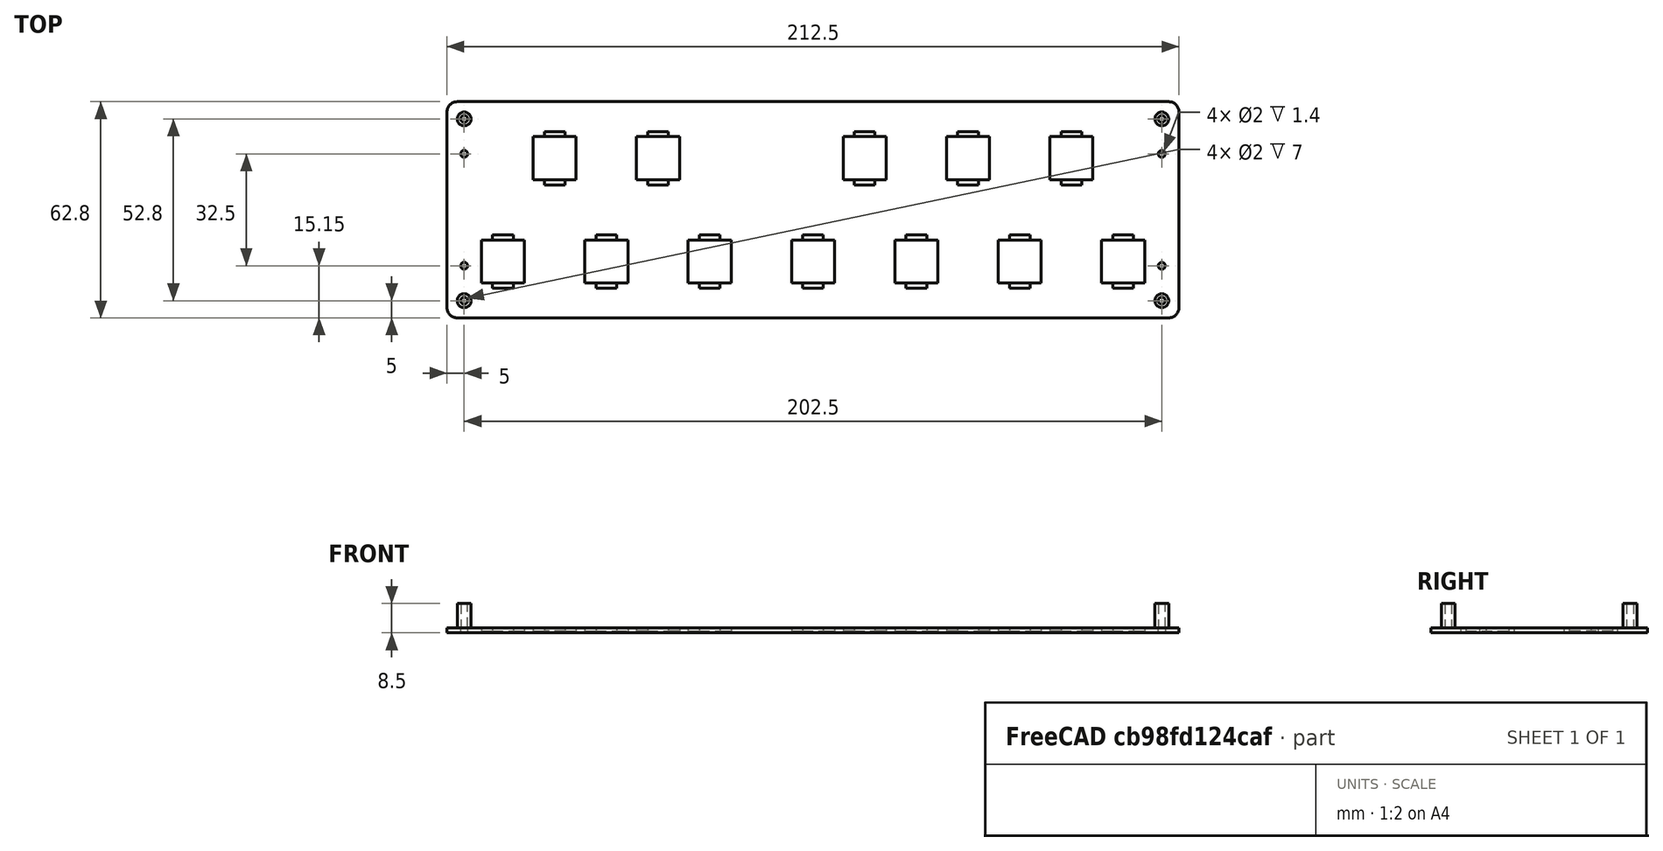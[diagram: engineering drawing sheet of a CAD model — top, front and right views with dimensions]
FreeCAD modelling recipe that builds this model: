
FCSTD DOCUMENT  (FreeCAD 0.20R28671 (Git))
Label: soporte botones
License: All rights reserved
LicenseURL: http://en.wikipedia.org/wiki/All_rights_reserved
objects: TechDraw::DrawViewDimension×21, Sketcher::SketchObject×5, PartDesign::Pocket×3, PartDesign::Pad×2, TechDraw::DrawProjGroupItem×2, PartDesign::Fillet×1, PartDesign::Body×1, TechDraw::DrawSVGTemplate×1, TechDraw::DrawProjGroup×1, TechDraw::DrawPage×1
note: 18 computed .brp shape members not serialized (recipe doc carries the construction recipe); baked Part::Feature solids carry a one-line shape summary decoded from their .brp

FEATURE [Sketcher::SketchObject] Sketch
  FullyConstrained = true
  MapMode = 5
  Support = -> [XY_Plane]
  sketch-geometry (75):
    g0: LineSegment StartX=0 StartY=0 StartZ=0 EndX=30 EndY=0 EndZ=0
    g1: LineSegment StartX=30 StartY=0 StartZ=0 EndX=30 EndY=30 EndZ=0
    g2: LineSegment StartX=0 StartY=30 StartZ=0 EndX=0 EndY=0 EndZ=0
    g3: LineSegment StartX=0 StartY=30 StartZ=0 EndX=15 EndY=30 EndZ=0
    g4: LineSegment StartX=15 StartY=30 StartZ=0 EndX=30 EndY=30 EndZ=0
    g5: LineSegment StartX=6.25 StartY=-6.25 StartZ=0 EndX=6.25 EndY=6.25 EndZ=0
    g6: LineSegment StartX=6.25 StartY=6.25 StartZ=0 EndX=-6.25 EndY=6.25 EndZ=0
    g7: LineSegment StartX=-6.25 StartY=6.25 StartZ=0 EndX=-6.25 EndY=-6.25 EndZ=0
    g8: LineSegment StartX=-6.25 StartY=-6.25 StartZ=0 EndX=6.25 EndY=-6.25 EndZ=0
    g9: Circle CenterX=0 CenterY=0 CenterZ=0 NormalX=0 NormalY=0 NormalZ=1 AngleXU=0 Radius=8.83883
    g10: LineSegment StartX=23.75 StartY=-6.25 StartZ=0 EndX=36.25 EndY=-6.25 EndZ=0
    g11: LineSegment StartX=23.75 StartY=6.25 StartZ=0 EndX=23.75 EndY=-6.25 EndZ=0
    g12: LineSegment StartX=36.25 StartY=6.25 StartZ=0 EndX=23.75 EndY=6.25 EndZ=0
    g13: LineSegment StartX=36.25 StartY=-6.25 StartZ=0 EndX=36.25 EndY=6.25 EndZ=0
    g14: LineSegment StartX=-6.25 StartY=-6.25 StartZ=0 EndX=23.75 EndY=-6.25 EndZ=0
    g15: LineSegment StartX=53.75 StartY=-6.25 StartZ=0 EndX=66.25 EndY=-6.25 EndZ=0
    g16: LineSegment StartX=53.75 StartY=6.25 StartZ=0 EndX=53.75 EndY=-6.25 EndZ=0
    g17: LineSegment StartX=66.25 StartY=6.25 StartZ=0 EndX=53.75 EndY=6.25 EndZ=0
    g18: LineSegment StartX=66.25 StartY=-6.25 StartZ=0 EndX=66.25 EndY=6.25 EndZ=0
    g19: LineSegment StartX=23.75 StartY=-6.25 StartZ=0 EndX=53.75 EndY=-6.25 EndZ=0
    g20: LineSegment StartX=83.75 StartY=-6.25 StartZ=0 EndX=96.25 EndY=-6.25 EndZ=0
    g21: LineSegment StartX=83.75 StartY=6.25 StartZ=0 EndX=83.75 EndY=-6.25 EndZ=0
    g22: LineSegment StartX=96.25 StartY=6.25 StartZ=0 EndX=83.75 EndY=6.25 EndZ=0
    g23: LineSegment StartX=96.25 StartY=-6.25 StartZ=0 EndX=96.25 EndY=6.25 EndZ=0
    g24: LineSegment StartX=53.75 StartY=-6.25 StartZ=0 EndX=83.75 EndY=-6.25 EndZ=0
    g25: LineSegment StartX=113.75 StartY=-6.25 StartZ=0 EndX=126.25 EndY=-6.25 EndZ=0
    g26: LineSegment StartX=113.75 StartY=6.25 StartZ=0 EndX=113.75 EndY=-6.25 EndZ=0
    g27: LineSegment StartX=126.25 StartY=6.25 StartZ=0 EndX=113.75 EndY=6.25 EndZ=0
    g28: LineSegment StartX=126.25 StartY=-6.25 StartZ=0 EndX=126.25 EndY=6.25 EndZ=0
    g29: LineSegment StartX=83.75 StartY=-6.25 StartZ=0 EndX=113.75 EndY=-6.25 EndZ=0
    g30: LineSegment StartX=143.75 StartY=-6.25 StartZ=0 EndX=156.25 EndY=-6.25 EndZ=0
    g31: LineSegment StartX=143.75 StartY=6.25 StartZ=0 EndX=143.75 EndY=-6.25 EndZ=0
    g32: LineSegment StartX=156.25 StartY=6.25 StartZ=0 EndX=143.75 EndY=6.25 EndZ=0
    g33: LineSegment StartX=156.25 StartY=-6.25 StartZ=0 EndX=156.25 EndY=6.25 EndZ=0
    g34: LineSegment StartX=113.75 StartY=-6.25 StartZ=0 EndX=143.75 EndY=-6.25 EndZ=0
    g35: LineSegment StartX=173.75 StartY=-6.25 StartZ=0 EndX=186.25 EndY=-6.25 EndZ=0
    g36: LineSegment StartX=173.75 StartY=6.25 StartZ=0 EndX=173.75 EndY=-6.25 EndZ=0
    g37: LineSegment StartX=186.25 StartY=6.25 StartZ=0 EndX=173.75 EndY=6.25 EndZ=0
    g38: LineSegment StartX=186.25 StartY=-6.25 StartZ=0 EndX=186.25 EndY=6.25 EndZ=0
    g39: LineSegment StartX=143.75 StartY=-6.25 StartZ=0 EndX=173.75 EndY=-6.25 EndZ=0
    g40: LineSegment StartX=8.75 StartY=23.75 StartZ=0 EndX=8.75 EndY=36.25 EndZ=0
    g41: LineSegment StartX=8.75 StartY=36.25 StartZ=0 EndX=21.25 EndY=36.25 EndZ=0
    g42: LineSegment StartX=21.25 StartY=36.25 StartZ=0 EndX=21.25 EndY=23.75 EndZ=0
    g43: LineSegment StartX=21.25 StartY=23.75 StartZ=0 EndX=8.75 EndY=23.75 EndZ=0
    g44: GeomPoint X=15 Y=30 Z=0
    g45: LineSegment StartX=30 StartY=30 StartZ=0 EndX=45 EndY=30 EndZ=0
    g46: LineSegment StartX=45 StartY=30 StartZ=0 EndX=60 EndY=30 EndZ=0
    g47: LineSegment StartX=38.75 StartY=36.25 StartZ=0 EndX=38.75 EndY=23.75 EndZ=0
    g48: LineSegment StartX=38.75 StartY=23.75 StartZ=0 EndX=51.25 EndY=23.75 EndZ=0
    g49: LineSegment StartX=51.25 StartY=23.75 StartZ=0 EndX=51.25 EndY=36.25 EndZ=0
    g50: LineSegment StartX=51.25 StartY=36.25 StartZ=0 EndX=38.75 EndY=36.25 EndZ=0
    g51: GeomPoint X=45 Y=30 Z=0
    g52: LineSegment StartX=90 StartY=30 StartZ=0 EndX=105 EndY=30 EndZ=0
    g53: LineSegment StartX=105 StartY=30 StartZ=0 EndX=120 EndY=30 EndZ=0
    g54: LineSegment StartX=120 StartY=30 StartZ=0 EndX=135 EndY=30 EndZ=0
    g55: LineSegment StartX=135 StartY=30 StartZ=0 EndX=150 EndY=30 EndZ=0
    g56: LineSegment StartX=150 StartY=30 StartZ=0 EndX=165 EndY=30 EndZ=0
    g57: LineSegment StartX=165 StartY=30 StartZ=0 EndX=180 EndY=30 EndZ=0
    g58: LineSegment StartX=90 StartY=30 StartZ=0 EndX=75 EndY=30 EndZ=0
    g59: LineSegment StartX=75 StartY=30 StartZ=0 EndX=60 EndY=30 EndZ=0
    g60: LineSegment StartX=98.75 StartY=36.25 StartZ=0 EndX=98.75 EndY=23.75 EndZ=0
    g61: LineSegment StartX=98.75 StartY=23.75 StartZ=0 EndX=111.25 EndY=23.75 EndZ=0
    g62: LineSegment StartX=111.25 StartY=23.75 StartZ=0 EndX=111.25 EndY=36.25 EndZ=0
    g63: LineSegment StartX=111.25 StartY=36.25 StartZ=0 EndX=98.75 EndY=36.25 EndZ=0
    g64: GeomPoint X=105 Y=30 Z=0
    g65: LineSegment StartX=128.75 StartY=36.25 StartZ=0 EndX=128.75 EndY=23.75 EndZ=0
    g66: LineSegment StartX=128.75 StartY=23.75 StartZ=0 EndX=141.25 EndY=23.75 EndZ=0
    g67: LineSegment StartX=141.25 StartY=23.75 StartZ=0 EndX=141.25 EndY=36.25 EndZ=0
    g68: LineSegment StartX=141.25 StartY=36.25 StartZ=0 EndX=128.75 EndY=36.25 EndZ=0
    g69: GeomPoint X=135 Y=30 Z=0
    g70: LineSegment StartX=158.75 StartY=36.25 StartZ=0 EndX=158.75 EndY=23.75 EndZ=0
    g71: LineSegment StartX=158.75 StartY=23.75 StartZ=0 EndX=171.25 EndY=23.75 EndZ=0
    g72: LineSegment StartX=171.25 StartY=23.75 StartZ=0 EndX=171.25 EndY=36.25 EndZ=0
    g73: LineSegment StartX=171.25 StartY=36.25 StartZ=0 EndX=158.75 EndY=36.25 EndZ=0
    g74: GeomPoint X=165 Y=30 Z=0
  constraints (202):
    c: Coincident(g0,g1)
    c: Coincident(g2,g0)
    c: Horizontal(g0)
    c: Vertical(g1)
    c: Vertical(g2)
    c: Coincident(g0,g-1)
    c: Coincident(g3,g2)
    c: Horizontal(g3)
    c: Coincident(g4,g3)
    c: Coincident(g4,g1)
    c: Horizontal(g4)
    c: Equal(g4,g3)
    c: Coincident(g5,g6)
    c: Coincident(g6,g7)
    c: Coincident(g7,g8)
    c: Coincident(g8,g5)
    c: Equal(g5,g6)
    c: Equal(g5,g7)
    c: Equal(g5,g8)
    c: PointOnObject(g5,g9)
    c: PointOnObject(g6,g9)
    c: PointOnObject(g7,g9)
    c: PointOnObject(g8,g9)
    c: Coincident(g9,g-1)
    c: Horizontal(g6)
    c: DistanceY(g7,g7) = 12.5
    c: Coincident(g13,g12)
    c: Coincident(g12,g11)
    c: Coincident(g11,g10)
    c: Coincident(g10,g13)
    c: Equal(g13,g12)
    c: Equal(g13,g11)
    c: Equal(g13,g10)
    c: Horizontal(g12)
    c: Coincident(g8,g14)
    c: Coincident(g10,g14)
    c: Distance(g14) = 30
    c: Coincident(g18,g17)
    c: Coincident(g17,g16)
    c: Coincident(g16,g15)
    c: Coincident(g15,g18)
    c: Equal(g18,g17)
    c: Equal(g18,g16)
    c: Equal(g18,g15)
    c: Horizontal(g17)
    c: Coincident(g10,g19)
    c: Coincident(g15,g19)
    c: Equal(g14,g19)
    c: Parallel(g19,g14)
    c: Coincident(g23,g22)
    c: Coincident(g22,g21)
    c: Coincident(g21,g20)
    c: Coincident(g20,g23)
    c: Equal(g23,g22)
    c: Equal(g23,g21)
    c: Equal(g23,g20)
    c: Horizontal(g22)
    c: Coincident(g15,g24)
    c: Coincident(g20,g24)
    c: Equal(g14,g24)
    c: Parallel(g24,g14)
    c: Coincident(g28,g27)
    c: Coincident(g27,g26)
    c: Coincident(g26,g25)
    c: Coincident(g25,g28)
    c: Equal(g28,g27)
    c: Equal(g28,g26)
    c: Equal(g28,g25)
    c: Horizontal(g27)
    c: Coincident(g20,g29)
    c: Coincident(g25,g29)
    c: Equal(g14,g29)
    c: Parallel(g29,g14)
    c: Coincident(g33,g32)
    c: Coincident(g32,g31)
    c: Coincident(g31,g30)
    c: Coincident(g30,g33)
    c: Equal(g33,g32)
    c: Equal(g33,g31)
    c: Equal(g33,g30)
    c: Horizontal(g32)
    c: Coincident(g25,g34)
    c: Coincident(g30,g34)
    c: Equal(g14,g34)
    c: Parallel(g34,g14)
    c: Coincident(g38,g37)
    c: Coincident(g37,g36)
    c: Coincident(g36,g35)
    c: Coincident(g35,g38)
    c: Equal(g38,g37)
    c: Equal(g38,g36)
    c: Equal(g38,g35)
    c: Horizontal(g37)
    c: Coincident(g30,g39)
    c: Coincident(g35,g39)
    c: Equal(g14,g39)
    c: Parallel(g39,g14)
    c: Horizontal(g19)
    c: Vertical(g11)
    c: Vertical(g16)
    c: Vertical(g21)
    c: Vertical(g26)
    c: Vertical(g31)
    c: Vertical(g36)
    c: Equal(g5,g11)
    c: Equal(g11,g16)
    c: Equal(g16,g21)
    c: Equal(g21,g26)
    c: Equal(g26,g31)
    c: Equal(g31,g36)
    c: Equal(g14,g1)
    c: Equal(g0,g2)
    c: Coincident(g40,g41)
    c: Coincident(g41,g42)
    c: Coincident(g42,g43)
    c: Coincident(g43,g40)
    c: Horizontal(g41)
    c: Horizontal(g43)
    c: Vertical(g40)
    c: Vertical(g42)
    c: Symmetric(g41,g40,g44)
    c: Coincident(g44,g3)
    c: Equal(g43,g12)
    c: Equal(g41,g42)
    c: Horizontal(g45)
    c: Coincident(g46,g45)
    c: Equal(g46,g45)
    c: Equal(g45,g3)
    c: Coincident(g45,g1)
    c: Horizontal(g46)
    c: Coincident(g47,g48)
    c: Coincident(g48,g49)
    c: Coincident(g49,g50)
    c: Coincident(g50,g47)
    c: Horizontal(g48)
    c: Horizontal(g50)
    c: Vertical(g47)
    c: Vertical(g49)
    c: Symmetric(g48,g47,g51)
    c: Coincident(g51,g45)
    c: Equal(g42,g50)
    c: Equal(g47,g50)
    c: Horizontal(g52)
    c: Coincident(g52,g53)
    c: Horizontal(g53)
    c: Coincident(g53,g54)
    c: Horizontal(g54)
    c: Coincident(g54,g55)
    c: Horizontal(g55)
    c: Coincident(g55,g56)
    c: Horizontal(g56)
    c: Coincident(g56,g57)
    c: Horizontal(g57)
    c: Equal(g46,g52)
    c: Equal(g52,g53)
    c: Equal(g53,g54)
    c: Equal(g54,g55)
    c: Equal(g55,g56)
    c: Equal(g56,g57)
    c: Horizontal(g52,g46)
    c: Coincident(g52,g58)
    c: Horizontal(g58)
    c: Coincident(g58,g59)
    c: Coincident(g59,g46)
    c: Equal(g59,g58)
    c: Equal(g58,g52)
    c: Coincident(g60,g61)
    c: Coincident(g61,g62)
    c: Coincident(g62,g63)
    c: Coincident(g63,g60)
    c: Horizontal(g61)
    c: Horizontal(g63)
    c: Vertical(g60)
    c: Vertical(g62)
    c: Symmetric(g61,g60,g64)
    c: Coincident(g65,g66)
    c: Coincident(g66,g67)
    c: Coincident(g67,g68)
    c: Coincident(g68,g65)
    c: Horizontal(g66)
    c: Horizontal(g68)
    c: Vertical(g65)
    c: Vertical(g67)
    c: Symmetric(g66,g65,g69)
    c: Coincident(g69,g54)
    c: Coincident(g70,g71)
    c: Coincident(g71,g72)
    c: Coincident(g72,g73)
    c: Coincident(g73,g70)
    c: Horizontal(g71)
    c: Horizontal(g73)
    c: Vertical(g70)
    c: Vertical(g72)
    c: Symmetric(g71,g70,g74)
    c: Coincident(g74,g56)
    c: Equal(g63,g62)
    c: Equal(g62,g68)
    c: Equal(g68,g65)
    c: Equal(g65,g73)
    c: Equal(g73,g70)
    c: Equal(g70,g13)
    c: Coincident(g64,g52)
FEATURE [Sketcher::SketchObject] Sketch001
  ExternalGeometry = -> [Sketch]
  FullyConstrained = true
  MapMode = 5
  Support = -> [XY_Plane]
  sketch-geometry (8):
    g0: LineSegment StartX=-16.25 StartY=46.4 StartZ=0 EndX=196.25 EndY=46.4 EndZ=0
    g1: LineSegment StartX=196.25 StartY=46.4 StartZ=0 EndX=196.25 EndY=-16.4 EndZ=0
    g2: LineSegment StartX=196.25 StartY=-16.4 StartZ=0 EndX=-16.25 EndY=-16.4 EndZ=0
    g3: LineSegment StartX=-16.25 StartY=-16.4 StartZ=0 EndX=-16.25 EndY=46.4 EndZ=0
    g4: LineSegment StartX=-6.25 StartY=-6.25 StartZ=0 EndX=-6.25 EndY=-16.4 EndZ=0
    g5: LineSegment StartX=-6.25 StartY=-6.25 StartZ=0 EndX=-16.25 EndY=-6.25 EndZ=0
    g6: LineSegment StartX=186.25 StartY=-6.25 StartZ=0 EndX=196.25 EndY=-6.25 EndZ=0
    g7: LineSegment StartX=171.25 StartY=36.25 StartZ=0 EndX=171.25 EndY=46.4 EndZ=0
  constraints (24):
    c: Coincident(g0,g1)
    c: Coincident(g1,g2)
    c: Coincident(g2,g3)
    c: Coincident(g3,g0)
    c: Horizontal(g0)
    c: Horizontal(g2)
    c: Vertical(g1)
    c: Vertical(g3)
    c: Coincident(g4,g-3)
    c: PointOnObject(g4,g2)
    c: Vertical(g4)
    c: Coincident(g5,g4)
    c: PointOnObject(g5,g3)
    c: Horizontal(g5)
    c: Coincident(g6,g-4)
    c: PointOnObject(g6,g1)
    c: Coincident(g7,g-6)
    c: PointOnObject(g7,g0)
    c: Vertical(g7)
    c: Horizontal(g6)
    c: DistanceY(g4,g4) = 10.15
    c: DistanceX(g5,g4) = 10
    c: Equal(g6,g5)
    c: Equal(g4,g7)
FEATURE [PartDesign::Pad] Pad
  Direction = (0,0,1)
  Length = 1.5
  Length2 = 100
  Profile = -> Sketch001
  ReferenceAxis = -> Sketch001 [N_Axis]
  Reversed = true
  Type = 0
FEATURE [PartDesign::Pocket] Pocket
  BaseFeature = -> Pad
  Direction = (0,0,-1)
  Length = 1
  Length2 = 100
  Profile = -> Sketch
  Type = 0
FEATURE [Sketcher::SketchObject] Sketch002
  ExternalGeometry = -> [Pocket]
  FullyConstrained = true
  MapMode = 5
  Support = -> [Pocket]
  sketch-geometry (130):
    g0: LineSegment StartX=177 StartY=6.25 StartZ=0 EndX=183 EndY=6.25 EndZ=0
    g1: LineSegment StartX=183 StartY=6.25 StartZ=0 EndX=183 EndY=7.75 EndZ=0
    g2: LineSegment StartX=183 StartY=7.75 StartZ=0 EndX=177 EndY=7.75 EndZ=0
    g3: LineSegment StartX=177 StartY=7.75 StartZ=0 EndX=177 EndY=6.25 EndZ=0
    g4: LineSegment StartX=177 StartY=-6.25 StartZ=0 EndX=183 EndY=-6.25 EndZ=0
    g5: LineSegment StartX=183 StartY=-6.25 StartZ=0 EndX=183 EndY=-7.75 EndZ=0
    g6: LineSegment StartX=183 StartY=-7.75 StartZ=0 EndX=177 EndY=-7.75 EndZ=0
    g7: LineSegment StartX=177 StartY=-7.75 StartZ=0 EndX=177 EndY=-6.25 EndZ=0
    g8: LineSegment StartX=177 StartY=6.25 StartZ=0 EndX=186.25 EndY=6.25 EndZ=0
    g9: LineSegment StartX=183 StartY=6.25 StartZ=0 EndX=173.75 EndY=6.25 EndZ=0
    g10: LineSegment StartX=153 StartY=-7.75 StartZ=0 EndX=147 EndY=-7.75 EndZ=0
    g11: LineSegment StartX=147 StartY=-7.75 StartZ=0 EndX=147 EndY=-6.25 EndZ=0
    g12: LineSegment StartX=147 StartY=-6.25 StartZ=0 EndX=153 EndY=-6.25 EndZ=0
    g13: LineSegment StartX=153 StartY=-6.25 StartZ=0 EndX=153 EndY=-7.75 EndZ=0
    g14: LineSegment StartX=147 StartY=6.25 StartZ=0 EndX=153 EndY=6.25 EndZ=0
    g15: LineSegment StartX=147 StartY=7.75 StartZ=0 EndX=147 EndY=6.25 EndZ=0
    g16: LineSegment StartX=153 StartY=7.75 StartZ=0 EndX=147 EndY=7.75 EndZ=0
    g17: LineSegment StartX=153 StartY=6.25 StartZ=0 EndX=153 EndY=7.75 EndZ=0
    g18: LineSegment StartX=183 StartY=-7.75 StartZ=0 EndX=153 EndY=-7.75 EndZ=0
    g19: LineSegment StartX=123 StartY=-7.75 StartZ=0 EndX=117 EndY=-7.75 EndZ=0
    g20: LineSegment StartX=117 StartY=-7.75 StartZ=0 EndX=117 EndY=-6.25 EndZ=0
    g21: LineSegment StartX=117 StartY=-6.25 StartZ=0 EndX=123 EndY=-6.25 EndZ=0
    g22: LineSegment StartX=123 StartY=-6.25 StartZ=0 EndX=123 EndY=-7.75 EndZ=0
    g23: LineSegment StartX=117 StartY=6.25 StartZ=0 EndX=123 EndY=6.25 EndZ=0
    g24: LineSegment StartX=117 StartY=7.75 StartZ=0 EndX=117 EndY=6.25 EndZ=0
    g25: LineSegment StartX=123 StartY=7.75 StartZ=0 EndX=117 EndY=7.75 EndZ=0
    g26: LineSegment StartX=123 StartY=6.25 StartZ=0 EndX=123 EndY=7.75 EndZ=0
    g27: LineSegment StartX=153 StartY=-7.75 StartZ=0 EndX=123 EndY=-7.75 EndZ=0
    g28: LineSegment StartX=93 StartY=-7.75 StartZ=0 EndX=87 EndY=-7.75 EndZ=0
    g29: LineSegment StartX=87 StartY=-7.75 StartZ=0 EndX=87 EndY=-6.25 EndZ=0
    g30: LineSegment StartX=87 StartY=-6.25 StartZ=0 EndX=93 EndY=-6.25 EndZ=0
    g31: LineSegment StartX=93 StartY=-6.25 StartZ=0 EndX=93 EndY=-7.75 EndZ=0
    g32: LineSegment StartX=87 StartY=6.25 StartZ=0 EndX=93 EndY=6.25 EndZ=0
    g33: LineSegment StartX=87 StartY=7.75 StartZ=0 EndX=87 EndY=6.25 EndZ=0
    g34: LineSegment StartX=93 StartY=7.75 StartZ=0 EndX=87 EndY=7.75 EndZ=0
    g35: LineSegment StartX=93 StartY=6.25 StartZ=0 EndX=93 EndY=7.75 EndZ=0
    g36: LineSegment StartX=123 StartY=-7.75 StartZ=0 EndX=93 EndY=-7.75 EndZ=0
    g37: LineSegment StartX=63 StartY=-7.75 StartZ=0 EndX=57 EndY=-7.75 EndZ=0
    g38: LineSegment StartX=57 StartY=-7.75 StartZ=0 EndX=57 EndY=-6.25 EndZ=0
    g39: LineSegment StartX=57 StartY=-6.25 StartZ=0 EndX=63 EndY=-6.25 EndZ=0
    g40: LineSegment StartX=63 StartY=-6.25 StartZ=0 EndX=63 EndY=-7.75 EndZ=0
    g41: LineSegment StartX=57 StartY=6.25 StartZ=0 EndX=63 EndY=6.25 EndZ=0
    g42: LineSegment StartX=57 StartY=7.75 StartZ=0 EndX=57 EndY=6.25 EndZ=0
    g43: LineSegment StartX=63 StartY=7.75 StartZ=0 EndX=57 EndY=7.75 EndZ=0
    g44: LineSegment StartX=63 StartY=6.25 StartZ=0 EndX=63 EndY=7.75 EndZ=0
    g45: LineSegment StartX=93 StartY=-7.75 StartZ=0 EndX=63 EndY=-7.75 EndZ=0
    g46: LineSegment StartX=93 StartY=-7.75 StartZ=0 EndX=87 EndY=-7.75 EndZ=0
    g47: LineSegment StartX=87 StartY=-7.75 StartZ=0 EndX=87 EndY=-6.25 EndZ=0
    g48: LineSegment StartX=87 StartY=-6.25 StartZ=0 EndX=93 EndY=-6.25 EndZ=0
    g49: LineSegment StartX=93 StartY=-6.25 StartZ=0 EndX=93 EndY=-7.75 EndZ=0
    g50: LineSegment StartX=87 StartY=6.25 StartZ=0 EndX=93 EndY=6.25 EndZ=0
    g51: LineSegment StartX=87 StartY=7.75 StartZ=0 EndX=87 EndY=6.25 EndZ=0
    g52: LineSegment StartX=93 StartY=7.75 StartZ=0 EndX=87 EndY=7.75 EndZ=0
    g53: LineSegment StartX=93 StartY=6.25 StartZ=0 EndX=93 EndY=7.75 EndZ=0
    g54: LineSegment StartX=63 StartY=-7.75 StartZ=0 EndX=93 EndY=-7.75 EndZ=0
    g55: LineSegment StartX=63 StartY=-7.75 StartZ=0 EndX=57 EndY=-7.75 EndZ=0
    g56: LineSegment StartX=57 StartY=-7.75 StartZ=0 EndX=57 EndY=-6.25 EndZ=0
    g57: LineSegment StartX=57 StartY=-6.25 StartZ=0 EndX=63 EndY=-6.25 EndZ=0
    g58: LineSegment StartX=63 StartY=-6.25 StartZ=0 EndX=63 EndY=-7.75 EndZ=0
    g59: LineSegment StartX=57 StartY=6.25 StartZ=0 EndX=63 EndY=6.25 EndZ=0
    g60: LineSegment StartX=57 StartY=7.75 StartZ=0 EndX=57 EndY=6.25 EndZ=0
    g61: LineSegment StartX=63 StartY=7.75 StartZ=0 EndX=57 EndY=7.75 EndZ=0
    g62: LineSegment StartX=63 StartY=6.25 StartZ=0 EndX=63 EndY=7.75 EndZ=0
    g63: LineSegment StartX=93 StartY=-7.75 StartZ=0 EndX=63 EndY=-7.75 EndZ=0
    g64: LineSegment StartX=156.25 StartY=-6.25 StartZ=0 EndX=147 EndY=-6.25 EndZ=0
    g65: LineSegment StartX=168 StartY=37.75 StartZ=0 EndX=162 EndY=37.75 EndZ=0
    g66: LineSegment StartX=162 StartY=37.75 StartZ=0 EndX=162 EndY=36.25 EndZ=0
    g67: LineSegment StartX=162 StartY=36.25 StartZ=0 EndX=168 EndY=36.25 EndZ=0
    g68: LineSegment StartX=168 StartY=36.25 StartZ=0 EndX=168 EndY=37.75 EndZ=0
    g69: LineSegment StartX=162 StartY=23.75 StartZ=0 EndX=168 EndY=23.75 EndZ=0
    g70: LineSegment StartX=162 StartY=22.25 StartZ=0 EndX=162 EndY=23.75 EndZ=0
    g71: LineSegment StartX=168 StartY=22.25 StartZ=0 EndX=162 EndY=22.25 EndZ=0
    g72: LineSegment StartX=168 StartY=23.75 StartZ=0 EndX=168 EndY=22.25 EndZ=0
    g73: LineSegment StartX=138 StartY=37.75 StartZ=0 EndX=132 EndY=37.75 EndZ=0
    g74: LineSegment StartX=132 StartY=37.75 StartZ=0 EndX=132 EndY=36.25 EndZ=0
    g75: LineSegment StartX=132 StartY=36.25 StartZ=0 EndX=138 EndY=36.25 EndZ=0
    g76: LineSegment StartX=138 StartY=36.25 StartZ=0 EndX=138 EndY=37.75 EndZ=0
    g77: LineSegment StartX=132 StartY=23.75 StartZ=0 EndX=138 EndY=23.75 EndZ=0
    g78: LineSegment StartX=132 StartY=22.25 StartZ=0 EndX=132 EndY=23.75 EndZ=0
    g79: LineSegment StartX=138 StartY=22.25 StartZ=0 EndX=132 EndY=22.25 EndZ=0
    g80: LineSegment StartX=138 StartY=23.75 StartZ=0 EndX=138 EndY=22.25 EndZ=0
    g81: LineSegment StartX=168 StartY=23.75 StartZ=0 EndX=171.25 EndY=23.75 EndZ=0
    g82: LineSegment StartX=158.75 StartY=23.75 StartZ=0 EndX=162 EndY=23.75 EndZ=0
    g83: LineSegment StartX=138 StartY=36.25 StartZ=0 EndX=141.25 EndY=36.25 EndZ=0
    g84: LineSegment StartX=27 StartY=7.75 StartZ=0 EndX=27 EndY=6.25 EndZ=0
    g85: LineSegment StartX=27 StartY=6.25 StartZ=0 EndX=33 EndY=6.25 EndZ=0
    g86: LineSegment StartX=33 StartY=7.75 StartZ=0 EndX=27 EndY=7.75 EndZ=0
    g87: LineSegment StartX=33 StartY=6.25 StartZ=0 EndX=33 EndY=7.75 EndZ=0
    g88: LineSegment StartX=33 StartY=-7.75 StartZ=0 EndX=27 EndY=-7.75 EndZ=0
    g89: LineSegment StartX=27 StartY=-7.75 StartZ=0 EndX=27 EndY=-6.25 EndZ=0
    g90: LineSegment StartX=27 StartY=-6.25 StartZ=0 EndX=33 EndY=-6.25 EndZ=0
    g91: LineSegment StartX=33 StartY=-6.25 StartZ=0 EndX=33 EndY=-7.75 EndZ=0
    g92: LineSegment StartX=-3 StartY=7.75 StartZ=0 EndX=-3 EndY=6.25 EndZ=0
    g93: LineSegment StartX=-3 StartY=6.25 StartZ=0 EndX=3 EndY=6.25 EndZ=0
    g94: LineSegment StartX=3 StartY=7.75 StartZ=0 EndX=-3 EndY=7.75 EndZ=0
    g95: LineSegment StartX=3 StartY=6.25 StartZ=0 EndX=3 EndY=7.75 EndZ=0
    g96: LineSegment StartX=3 StartY=-7.75 StartZ=0 EndX=-3 EndY=-7.75 EndZ=0
    g97: LineSegment StartX=-3 StartY=-7.75 StartZ=0 EndX=-3 EndY=-6.25 EndZ=0
    g98: LineSegment StartX=-3 StartY=-6.25 StartZ=0 EndX=3 EndY=-6.25 EndZ=0
    g99: LineSegment StartX=3 StartY=-6.25 StartZ=0 EndX=3 EndY=-7.75 EndZ=0
    g100: LineSegment StartX=63 StartY=-7.75 StartZ=0 EndX=33 EndY=-7.75 EndZ=0
    g101: LineSegment StartX=33 StartY=-7.75 StartZ=0 EndX=3 EndY=-7.75 EndZ=0
    g102: LineSegment StartX=108 StartY=36.25 StartZ=0 EndX=102 EndY=36.25 EndZ=0
    g103: LineSegment StartX=102 StartY=37.75 StartZ=0 EndX=108 EndY=37.75 EndZ=0
    g104: LineSegment StartX=108 StartY=37.75 StartZ=0 EndX=108 EndY=36.25 EndZ=0
    g105: LineSegment StartX=102 StartY=36.25 StartZ=0 EndX=102 EndY=37.75 EndZ=0
    g106: LineSegment StartX=102 StartY=22.25 StartZ=0 EndX=108 EndY=22.25 EndZ=0
    g107: LineSegment StartX=108 StartY=23.75 StartZ=0 EndX=102 EndY=23.75 EndZ=0
    g108: LineSegment StartX=102 StartY=23.75 StartZ=0 EndX=102 EndY=22.25 EndZ=0
    g109: LineSegment StartX=108 StartY=22.25 StartZ=0 EndX=108 EndY=23.75 EndZ=0
    g110: LineSegment StartX=108 StartY=23.75 StartZ=0 EndX=111.25 EndY=23.75 EndZ=0
    g111: LineSegment StartX=183 StartY=-6.25 StartZ=0 EndX=168 EndY=23.75 EndZ=0
    g112: LineSegment StartX=42 StartY=37.75 StartZ=0 EndX=48 EndY=37.75 EndZ=0
    g113: LineSegment StartX=48 StartY=36.25 StartZ=0 EndX=42 EndY=36.25 EndZ=0
    g114: LineSegment StartX=42 StartY=36.25 StartZ=0 EndX=42 EndY=37.75 EndZ=0
    g115: LineSegment StartX=48 StartY=37.75 StartZ=0 EndX=48 EndY=36.25 EndZ=0
    g116: LineSegment StartX=48 StartY=23.75 StartZ=0 EndX=42 EndY=23.75 EndZ=0
    g117: LineSegment StartX=42 StartY=22.25 StartZ=0 EndX=48 EndY=22.25 EndZ=0
    g118: LineSegment StartX=48 StartY=22.25 StartZ=0 EndX=48 EndY=23.75 EndZ=0
    g119: LineSegment StartX=42 StartY=23.75 StartZ=0 EndX=42 EndY=22.25 EndZ=0
    g120: LineSegment StartX=48 StartY=36.25 StartZ=0 EndX=51.25 EndY=36.25 EndZ=0
    g121: LineSegment StartX=18 StartY=23.75 StartZ=0 EndX=12 EndY=23.75 EndZ=0
    g122: LineSegment StartX=18 StartY=22.25 StartZ=0 EndX=18 EndY=23.75 EndZ=0
    g123: LineSegment StartX=12 StartY=22.25 StartZ=0 EndX=18 EndY=22.25 EndZ=0
    g124: LineSegment StartX=12 StartY=23.75 StartZ=0 EndX=12 EndY=22.25 EndZ=0
    g125: LineSegment StartX=18 StartY=36.25 StartZ=0 EndX=12 EndY=36.25 EndZ=0
    g126: LineSegment StartX=12 StartY=37.75 StartZ=0 EndX=18 EndY=37.75 EndZ=0
    g127: LineSegment StartX=18 StartY=37.75 StartZ=0 EndX=18 EndY=36.25 EndZ=0
    g128: LineSegment StartX=12 StartY=36.25 StartZ=0 EndX=12 EndY=37.75 EndZ=0
    g129: LineSegment StartX=18 StartY=36.25 StartZ=0 EndX=21.25 EndY=36.25 EndZ=0
  constraints (372):
    c: Coincident(g0,g1)
    c: Coincident(g1,g2)
    c: Coincident(g2,g3)
    c: Coincident(g3,g0)
    c: Horizontal(g0)
    c: Horizontal(g2)
    c: Vertical(g1)
    c: Vertical(g3)
    c: Coincident(g4,g5)
    c: Coincident(g5,g6)
    c: Coincident(g6,g7)
    c: Coincident(g7,g4)
    c: Horizontal(g4)
    c: Horizontal(g6)
    c: Vertical(g5)
    c: Vertical(g7)
    c: Coincident(g8,g0)
    c: Coincident(g8,g-3)
    c: Coincident(g9,g0)
    c: Coincident(g9,g-4)
    c: Equal(g9,g8)
    c: Equal(g0,g4)
    c: DistanceX(g2,g2) = 6
    c: DistanceY(g3,g3) = 1.5
    c: Horizontal(g9)
    c: Equal(g5,g1)
    c: Horizontal(g4,g-5)
    c: Coincident(g14,g17)
    c: Coincident(g17,g16)
    c: Coincident(g16,g15)
    c: Coincident(g15,g14)
    c: Horizontal(g14)
    c: Horizontal(g16)
    c: Vertical(g17)
    c: Vertical(g15)
    c: Coincident(g12,g13)
    c: Coincident(g13,g10)
    c: Coincident(g10,g11)
    c: Coincident(g11,g12)
    c: Horizontal(g12)
    c: Horizontal(g10)
    c: Vertical(g13)
    c: Vertical(g11)
    c: Vertical(g12,g14)
    c: Equal(g14,g12)
    c: Equal(g13,g17)
    c: Coincident(g6,g18)
    c: Coincident(g10,g18)
    c: Coincident(g23,g26)
    c: Coincident(g26,g25)
    c: Coincident(g25,g24)
    c: Coincident(g24,g23)
    c: Horizontal(g23)
    c: Horizontal(g25)
    c: Vertical(g26)
    c: Vertical(g24)
    c: Coincident(g21,g22)
    c: Coincident(g22,g19)
    c: Coincident(g19,g20)
    c: Coincident(g20,g21)
    c: Horizontal(g21)
    c: Horizontal(g19)
    c: Vertical(g22)
    c: Vertical(g20)
    c: Vertical(g21,g23)
    c: Equal(g23,g21)
    c: Equal(g22,g26)
    c: Coincident(g10,g27)
    c: Coincident(g19,g27)
    c: Equal(g18,g27)
    c: Parallel(g27,g18)
    c: Coincident(g32,g35)
    c: Coincident(g35,g34)
    c: Coincident(g34,g33)
    c: Coincident(g33,g32)
    c: Horizontal(g32)
    c: Horizontal(g34)
    c: Vertical(g35)
    c: Vertical(g33)
    c: Coincident(g30,g31)
    c: Coincident(g31,g28)
    c: Coincident(g28,g29)
    c: Coincident(g29,g30)
    c: Horizontal(g30)
    c: Horizontal(g28)
    c: Vertical(g31)
    c: Vertical(g29)
    c: Vertical(g30,g32)
    c: Equal(g32,g30)
    c: Equal(g31,g35)
    c: Coincident(g19,g36)
    c: Coincident(g28,g36)
    c: Equal(g18,g36)
    c: Parallel(g36,g18)
    c: Coincident(g41,g44)
    c: Coincident(g44,g43)
    c: Coincident(g43,g42)
    c: Coincident(g42,g41)
    c: Horizontal(g41)
    c: Horizontal(g43)
    c: Vertical(g44)
    c: Vertical(g42)
    c: Coincident(g39,g40)
    c: Coincident(g40,g37)
    c: Coincident(g37,g38)
    c: Coincident(g38,g39)
    c: Horizontal(g39)
    c: Horizontal(g37)
    c: Vertical(g40)
    c: Vertical(g38)
    c: Vertical(g39,g41)
    c: Equal(g41,g39)
    c: Equal(g40,g44)
    c: Coincident(g28,g45)
    c: Coincident(g37,g45)
    c: Equal(g18,g45)
    c: Parallel(g45,g18)
    c: Coincident(g50,g53)
    c: Coincident(g53,g52)
    c: Coincident(g52,g51)
    c: Coincident(g51,g50)
    c: Horizontal(g50)
    c: Horizontal(g52)
    c: Vertical(g53)
    c: Vertical(g51)
    c: Coincident(g48,g49)
    c: Coincident(g49,g46)
    c: Coincident(g46,g47)
    c: Coincident(g47,g48)
    c: Horizontal(g48)
    c: Horizontal(g46)
    c: Vertical(g49)
    c: Vertical(g47)
    c: Vertical(g48,g50)
    c: Equal(g50,g48)
    c: Equal(g49,g53)
    c: Coincident(g37,g54)
    c: Coincident(g46,g54)
    c: Equal(g18,g54)
    c: Parallel(g54,g18)
    c: Coincident(g59,g62)
    c: Coincident(g62,g61)
    c: Coincident(g61,g60)
    c: Coincident(g60,g59)
    c: Horizontal(g59)
    c: Horizontal(g61)
    c: Vertical(g62)
    c: Vertical(g60)
    c: Coincident(g57,g58)
    c: Coincident(g58,g55)
    c: Coincident(g55,g56)
    c: Coincident(g56,g57)
    c: Horizontal(g57)
    c: Horizontal(g55)
    c: Vertical(g58)
    c: Vertical(g56)
    c: Vertical(g57,g59)
    c: Equal(g59,g57)
    c: Equal(g58,g62)
    c: Coincident(g46,g63)
    c: Coincident(g55,g63)
    c: Equal(g18,g63)
    c: Parallel(g63,g18)
    c: Horizontal(g14,g9)
    c: Horizontal(g14,g23)
    c: Horizontal(g23,g32)
    c: Horizontal(g32,g41)
    c: Horizontal(g41,g50)
    c: Horizontal(g50,g59)
    c: Equal(g2,g16)
    c: Equal(g16,g25)
    c: Equal(g25,g34)
    c: Equal(g34,g43)
    c: Equal(g43,g52)
    c: Equal(g61,g2)
    c: Equal(g60,g51)
    c: Equal(g51,g42)
    c: Equal(g42,g33)
    c: Equal(g33,g24)
    c: Equal(g24,g15)
    c: Equal(g15,g1)
    c: Horizontal(g18)
    c: Coincident(g64,g-7)
    c: Coincident(g64,g11)
    c: Equal(g64,g9)
    c: Coincident(g69,g72)
    c: Coincident(g72,g71)
    c: Coincident(g71,g70)
    c: Coincident(g70,g69)
    c: Horizontal(g69)
    c: Horizontal(g71)
    c: Vertical(g72)
    c: Vertical(g70)
    c: Coincident(g67,g68)
    c: Coincident(g68,g65)
    c: Coincident(g65,g66)
    c: Coincident(g66,g67)
    c: Horizontal(g67)
    c: Horizontal(g65)
    c: Vertical(g68)
    c: Vertical(g66)
    c: Vertical(g67,g69)
    c: Equal(g69,g67)
    c: Coincident(g77,g80)
    c: Coincident(g80,g79)
    c: Coincident(g79,g78)
    c: Coincident(g78,g77)
    c: Horizontal(g77)
    c: Horizontal(g79)
    c: Vertical(g80)
    c: Vertical(g78)
    c: Coincident(g75,g76)
    c: Coincident(g76,g73)
    c: Coincident(g73,g74)
    c: Coincident(g74,g75)
    c: Horizontal(g75)
    c: Horizontal(g73)
    c: Vertical(g76)
    c: Vertical(g74)
    c: Vertical(g75,g77)
    c: Equal(g77,g75)
    c: Equal(g76,g80)
    c: Horizontal(g69,g77)
    c: Equal(g71,g79)
    c: Equal(g78,g70)
    c: Horizontal(g67,g-8)
    c: Horizontal(g-9,g69)
    c: Horizontal(g74,g67)
    c: Coincident(g81,g69)
    c: Coincident(g81,g-9)
    c: Coincident(g82,g-10)
    c: Coincident(g82,g69)
    c: Equal(g82,g81)
    c: Equal(g71,g0)
    c: Vertical(g0,g4)
    c: Coincident(g83,g75)
    c: Coincident(g83,g-11)
    c: Equal(g83,g82)
    c: Coincident(g85,g87)
    c: Coincident(g87,g86)
    c: Coincident(g86,g84)
    c: Coincident(g84,g85)
    c: Horizontal(g85)
    c: Horizontal(g86)
    c: Vertical(g87)
    c: Vertical(g84)
    c: Coincident(g90,g91)
    c: Coincident(g91,g88)
    c: Coincident(g88,g89)
    c: Coincident(g89,g90)
    c: Horizontal(g90)
    c: Horizontal(g88)
    c: Vertical(g91)
    c: Vertical(g89)
    c: Vertical(g90,g85)
    c: Equal(g85,g90)
    c: Equal(g91,g87)
    c: Coincident(g93,g95)
    c: Coincident(g95,g94)
    c: Coincident(g94,g92)
    c: Coincident(g92,g93)
    c: Horizontal(g93)
    c: Horizontal(g94)
    c: Vertical(g95)
    c: Vertical(g92)
    c: Coincident(g98,g99)
    c: Coincident(g99,g96)
    c: Coincident(g96,g97)
    c: Coincident(g97,g98)
    c: Horizontal(g98)
    c: Horizontal(g96)
    c: Vertical(g99)
    c: Vertical(g97)
    c: Vertical(g98,g93)
    c: Equal(g93,g98)
    c: Equal(g99,g95)
    c: Horizontal(g90,g38)
    c: Coincident(g100,g37)
    c: Coincident(g100,g88)
    c: Horizontal(g100)
    c: Coincident(g101,g88)
    c: Coincident(g101,g96)
    c: Horizontal(g101)
    c: Equal(g101,g100)
    c: Equal(g100,g45)
    c: Equal(g90,g37)
    c: Equal(g37,g98)
    c: Horizontal(g98,g89)
    c: Horizontal(g85,g41)
    c: Horizontal(g93,g85)
    c: Coincident(g107,g108)
    c: Coincident(g108,g106)
    c: Coincident(g106,g109)
    c: Coincident(g109,g107)
    c: Horizontal(g107)
    c: Horizontal(g106)
    c: Vertical(g108)
    c: Vertical(g109)
    c: Coincident(g102,g105)
    c: Coincident(g105,g103)
    c: Coincident(g103,g104)
    c: Coincident(g104,g102)
    c: Horizontal(g102)
    c: Horizontal(g103)
    c: Vertical(g105)
    c: Vertical(g104)
    c: Vertical(g102,g107)
    c: Equal(g107,g102)
    c: Equal(g105,g108)
    c: Equal(g70,g66)
    c: Equal(g70,g3)
    c: Horizontal(g102,g74)
    c: Horizontal(g107,g77)
    c: Equal(g106,g79)
    c: Horizontal(g78,g106)
    c: Coincident(g110,g107)
    c: Coincident(g110,g-12)
    c: Equal(g110,g83)
    c: Coincident(g111,g4)
    c: Coincident(g111,g69)
    c: Coincident(g116,g119)
    c: Coincident(g119,g117)
    c: Coincident(g117,g118)
    c: Coincident(g118,g116)
    c: Horizontal(g116)
    c: Horizontal(g117)
    c: Vertical(g119)
    c: Vertical(g118)
    c: Coincident(g113,g114)
    c: Coincident(g114,g112)
    c: Coincident(g112,g115)
    c: Coincident(g115,g113)
    c: Horizontal(g113)
    c: Horizontal(g112)
    c: Vertical(g114)
    c: Vertical(g115)
    c: Vertical(g113,g116)
    c: Equal(g116,g113)
    c: Equal(g114,g119)
    c: Coincident(g120,g113)
    c: Coincident(g120,g-13)
    c: Horizontal(g120)
    c: Coincident(g121,g124)
    c: Coincident(g124,g123)
    c: Coincident(g123,g122)
    c: Coincident(g122,g121)
    c: Horizontal(g121)
    c: Horizontal(g123)
    c: Vertical(g124)
    c: Vertical(g122)
    c: Coincident(g125,g128)
    c: Coincident(g128,g126)
    c: Coincident(g126,g127)
    c: Coincident(g127,g125)
    c: Horizontal(g125)
    c: Horizontal(g126)
    c: Vertical(g128)
    c: Vertical(g127)
    c: Vertical(g125,g121)
    c: Equal(g121,g125)
    c: Equal(g128,g124)
    c: Coincident(g129,g125)
    c: Coincident(g129,g-14)
    c: Horizontal(g129)
    c: Equal(g129,g120)
    c: Equal(g120,g110)
    c: Horizontal(g116,g107)
    c: Horizontal(g121,g116)
    c: Equal(g117,g123)
    c: Equal(g123,g106)
    c: Equal(g122,g108)
    c: Equal(g122,g119)
FEATURE [PartDesign::Pocket] Pocket001
  BaseFeature = -> Pocket
  Direction = (0,0,-1)
  Length = 1.4
  Length2 = 100
  Profile = -> Sketch002
  Type = 1
FEATURE [Sketcher::SketchObject] Sketch003
  ExternalGeometry = -> [Pocket001]
  FullyConstrained = true
  MapMode = 5
  Support = -> [Pocket001]
  sketch-geometry (16):
    g0: Circle CenterX=-11.25 CenterY=41.4 CenterZ=0 NormalX=0 NormalY=0 NormalZ=1 AngleXU=0 Radius=2
    g1: Circle CenterX=-11.25 CenterY=41.4 CenterZ=0 NormalX=0 NormalY=0 NormalZ=1 AngleXU=0 Radius=1
    g2: LineSegment StartX=-16.25 StartY=46.4 StartZ=0 EndX=-16.25 EndY=41.4 EndZ=0
    g3: LineSegment StartX=-16.25 StartY=46.4 StartZ=0 EndX=-11.25 EndY=46.4 EndZ=0
    g4: LineSegment StartX=-16.25 StartY=-16.4 StartZ=0 EndX=-16.25 EndY=-11.4 EndZ=0
    g5: LineSegment StartX=-16.25 StartY=-16.4 StartZ=0 EndX=-11.25 EndY=-16.4 EndZ=0
    g6: Circle CenterX=-11.25 CenterY=-11.4 CenterZ=0 NormalX=0 NormalY=0 NormalZ=1 AngleXU=0 Radius=2
    g7: Circle CenterX=-11.25 CenterY=-11.4 CenterZ=0 NormalX=0 NormalY=0 NormalZ=1 AngleXU=0 Radius=1
    g8: LineSegment StartX=191.25 StartY=-16.4 StartZ=0 EndX=196.25 EndY=-16.4 EndZ=0
    g9: LineSegment StartX=196.25 StartY=-16.4 StartZ=0 EndX=196.25 EndY=-11.4 EndZ=0
    g10: LineSegment StartX=196.25 StartY=46.4 StartZ=0 EndX=196.25 EndY=41.4 EndZ=0
    g11: LineSegment StartX=196.25 StartY=46.4 StartZ=0 EndX=191.25 EndY=46.4 EndZ=0
    g12: Circle CenterX=191.25 CenterY=-11.4 CenterZ=0 NormalX=0 NormalY=0 NormalZ=1 AngleXU=0 Radius=1
    g13: Circle CenterX=191.25 CenterY=-11.4 CenterZ=0 NormalX=0 NormalY=0 NormalZ=1 AngleXU=0 Radius=2
    g14: Circle CenterX=191.25 CenterY=41.4 CenterZ=0 NormalX=0 NormalY=0 NormalZ=1 AngleXU=0 Radius=1
    g15: Circle CenterX=191.25 CenterY=41.4 CenterZ=0 NormalX=0 NormalY=0 NormalZ=1 AngleXU=0 Radius=2
  constraints (44):
    c: Coincident(g1,g0)
    c: Diameter(g1) = 2
    c: Diameter(g0) = 4
    c: Vertical(g2)
    c: Coincident(g3,g2)
    c: Horizontal(g0,g2)
    c: Horizontal(g3)
    c: Vertical(g0,g3)
    c: Equal(g2,g3)
    c: DistanceY(g2,g2) = 5
    c: Vertical(g4)
    c: Coincident(g5,g4)
    c: Horizontal(g5)
    c: Coincident(g7,g6)
    c: Horizontal(g6,g4)
    c: Vertical(g5,g6)
    c: Equal(g6,g0)
    c: Equal(g1,g7)
    c: Horizontal(g8)
    c: Coincident(g9,g8)
    c: Vertical(g9)
    c: Vertical(g10)
    c: Coincident(g11,g10)
    c: Horizontal(g11)
    c: Equal(g11,g10)
    c: Coincident(g13,g12)
    c: Coincident(g15,g14)
    c: Equal(g14,g12)
    c: Equal(g12,g7)
    c: Equal(g6,g13)
    c: Equal(g13,g15)
    c: Horizontal(g14,g10)
    c: Horizontal(g12,g9)
    c: Vertical(g8,g12)
    c: Vertical(g11,g14)
    c: Coincident(g4,g-3)
    c: Coincident(g8,g-3)
    c: Equal(g9,g8)
    c: Equal(g8,g5)
    c: Equal(g5,g4)
    c: Equal(g4,g2)
    c: Coincident(g2,g-4)
    c: Coincident(g10,g-5)
    c: Equal(g11,g3)
FEATURE [PartDesign::Pad] Pad001
  BaseFeature = -> Pocket001
  Direction = (0,0,1)
  Length = 7
  Length2 = 100
  Profile = -> Sketch003
  ReferenceAxis = -> Sketch003 [N_Axis]
  Type = 0
FEATURE [Sketcher::SketchObject] Sketch004
  ExternalGeometry = -> [Pad001]
  FullyConstrained = false
  MapMode = 5
  Support = -> [Pad001]
  sketch-geometry (8):
    g0: LineSegment StartX=-11.25 StartY=41.25 StartZ=0 EndX=-11.25 EndY=31.25 EndZ=0
    g1: LineSegment StartX=-11.25 StartY=-11.25 StartZ=0 EndX=-11.25 EndY=-1.25 EndZ=0
    g2: LineSegment StartX=191.25 StartY=-11.25 StartZ=0 EndX=191.25 EndY=-1.25 EndZ=0
    g3: LineSegment StartX=191.25 StartY=41.25 StartZ=0 EndX=191.25 EndY=31.25 EndZ=0
    g4: Circle CenterX=-11.25 CenterY=-1.25 CenterZ=0 NormalX=0 NormalY=0 NormalZ=1 AngleXU=0 Radius=1
    g5: Circle CenterX=-11.25 CenterY=31.25 CenterZ=0 NormalX=0 NormalY=0 NormalZ=1 AngleXU=0 Radius=1
    g6: Circle CenterX=191.25 CenterY=31.25 CenterZ=0 NormalX=0 NormalY=0 NormalZ=1 AngleXU=0 Radius=1
    g7: Circle CenterX=191.25 CenterY=-1.25 CenterZ=0 NormalX=0 NormalY=0 NormalZ=1 AngleXU=0 Radius=1
  constraints (16):
    c: Vertical(g0)
    c: Vertical(g1)
    c: Equal(g1,g0)
    c: Vertical(g2)
    c: Vertical(g3)
    c: Equal(g3,g2)
    c: Equal(g2,g0)
    c: Coincident(g4,g1)
    c: Coincident(g5,g0)
    c: Coincident(g6,g3)
    c: Coincident(g7,g2)
    c: Equal(g7,g6)
    c: Equal(g6,g5)
    c: Equal(g5,g4)
    c: Diameter(g5) = 2
    c: DistanceY(g1,g1) = 10
FEATURE [PartDesign::Pocket] Pocket002
  BaseFeature = -> Pad001
  Direction = (0,0,-1)
  Length = 1.4
  Length2 = 100
  Profile = -> Sketch004
  Type = 0
FEATURE [PartDesign::Fillet] Fillet
  Base = -> Pocket002 [Edge2,Edge8,Edge5,Edge1]
  BaseFeature = -> Pocket002
  Radius = 3
  SupportTransform = false
  UseAllEdges = false
FEATURE [PartDesign::Body] Body
  Group = -> [Sketch,Sketch001,Pad,Pocket,Sketch002,Pocket001,Sketch003,Pad001,Sketch004,Pocket002,Fillet]
  Origin = -> Origin
  Tip = -> Fillet
FEATURE [TechDraw::DrawSVGTemplate] Template
  EditableTexts = AUTHOR_NAME=Daniel García García; DATE=15-04-2022; DN=14; DOCUMENT_TYPE=Plano de Pieza; PN=21; REVISION=1; SCALE=1:1; SHEET=14/15; SIZE=A4; TITLELINE-1=Soporte de botones Arriba
  Height = 210
  Orientation = 1
  Width = 297
FEATURE [TechDraw::DrawProjGroupItem] ProjItem  label="Front"
  CoarseView = false
  Direction = (0,-1,0)
  Focus = 100
  HardHidden = false
  IsoCount = 0
  IsoHidden = false
  IsoVisible = false
  LockPosition = true
  Perspective = false
  Rotation = 0
  RotationVector = (1,0,0)
  ScaleType = 2
  SeamHidden = false
  SeamVisible = true
  SmoothHidden = false
  SmoothVisible = true
  Source = -> [Fillet]
  Type = 0
  X = 0
  XDirection = (1,0,0)
  Y = 0
FEATURE [TechDraw::DrawProjGroupItem] ProjItem001  label="Top"
  CoarseView = false
  Direction = (0,0,1)
  Focus = 100
  HardHidden = false
  IsoCount = 0
  IsoHidden = false
  IsoVisible = false
  LockPosition = true
  Perspective = false
  Rotation = 0
  RotationVector = (1,0,0)
  ScaleType = 2
  SeamHidden = false
  SeamVisible = true
  SmoothHidden = false
  SmoothVisible = true
  Source = -> [Fillet]
  Type = 4
  X = 0
  XDirection = (1,0,0)
  Y = -64.4611
FEATURE [TechDraw::DrawProjGroup] ProjGroup
  Anchor = -> ProjItem
  AutoDistribute = true
  LockPosition = true
  ProjectionType = 0
  Rotation = 0
  ScaleType = 0
  Source = -> [Fillet]
  Views = -> [ProjItem,ProjItem001]
  X = 153.996
  Y = 158.059
  spacingX = 15
  spacingY = 15
FEATURE [TechDraw::DrawViewDimension] Dimension
  AngleOverride = false
  Arbitrary = false
  ArbitraryTolerances = false
  EqualTolerance = true
  ExtensionAngle = 0
  FormatSpec = %.2w
  FormatSpecOverTolerance = %+.2w
  FormatSpecUnderTolerance = %+.2w
  Inverted = false
  LineAngle = 0
  LockPosition = false
  MeasureType = 1
  OverTolerance = 0
  References2D = -> [ProjItem]
  Rotation = 0
  ScaleType = 0
  TheoreticalExact = false
  Type = 1
  UnderTolerance = 0
  X = 1.98106
  Y = 23.0698
FEATURE [TechDraw::DrawViewDimension] Dimension001
  AngleOverride = false
  Arbitrary = false
  ArbitraryTolerances = false
  EqualTolerance = true
  ExtensionAngle = 0
  FormatSpec = %.2w
  FormatSpecOverTolerance = %+.2w
  FormatSpecUnderTolerance = %+.2w
  Inverted = false
  LineAngle = 0
  LockPosition = false
  MeasureType = 1
  OverTolerance = 0
  References2D = -> [ProjItem]
  Rotation = 0
  ScaleType = 0
  TheoreticalExact = false
  Type = 2
  UnderTolerance = 0
  X = -119.784
  Y = 6.50579
FEATURE [TechDraw::DrawViewDimension] Dimension002
  AngleOverride = false
  Arbitrary = false
  ArbitraryTolerances = false
  EqualTolerance = true
  ExtensionAngle = 0
  FormatSpec = %.2w
  FormatSpecOverTolerance = %+.2w
  FormatSpecUnderTolerance = %+.2w
  Inverted = false
  LineAngle = 0
  LockPosition = false
  MeasureType = 1
  OverTolerance = 0
  References2D = -> [ProjItem]
  Rotation = 0
  ScaleType = 0
  TheoreticalExact = false
  Type = 1
  UnderTolerance = 0
  X = -1.15904
  Y = -9.93145
FEATURE [TechDraw::DrawViewDimension] Dimension003
  AngleOverride = false
  Arbitrary = false
  ArbitraryTolerances = false
  EqualTolerance = true
  ExtensionAngle = 0
  FormatSpec = ∅%.2w
  FormatSpecOverTolerance = %+.2w
  FormatSpecUnderTolerance = %+.2w
  Inverted = false
  LineAngle = 0
  LockPosition = false
  MeasureType = 1
  OverTolerance = 0
  References2D = -> [ProjItem]
  Rotation = 0
  ScaleType = 0
  TheoreticalExact = false
  Type = 1
  UnderTolerance = 0
  X = -87.9019
  Y = 6.53471
FEATURE [TechDraw::DrawViewDimension] Dimension004
  AngleOverride = false
  Arbitrary = false
  ArbitraryTolerances = false
  EqualTolerance = true
  ExtensionAngle = 0
  FormatSpec = %.2w
  FormatSpecOverTolerance = %+.2w
  FormatSpecUnderTolerance = %+.2w
  Inverted = false
  LineAngle = 0
  LockPosition = false
  MeasureType = 1
  OverTolerance = 0
  References2D = -> [ProjItem001]
  Rotation = 0
  ScaleType = 0
  TheoreticalExact = false
  Type = 2
  UnderTolerance = 0
  X = 129.206
  Y = -0.255297
FEATURE [TechDraw::DrawViewDimension] Dimension005
  AngleOverride = false
  Arbitrary = false
  ArbitraryTolerances = false
  EqualTolerance = true
  ExtensionAngle = 0
  FormatSpec = ⌀%.2w
  FormatSpecOverTolerance = %+.2w
  FormatSpecUnderTolerance = %+.2w
  Inverted = false
  LineAngle = 0
  LockPosition = false
  MeasureType = 1
  OverTolerance = 0
  References2D = -> [ProjItem001]
  Rotation = 0
  ScaleType = 0
  TheoreticalExact = false
  Type = 5
  UnderTolerance = 0
  X = -118.313
  Y = -22.3404
FEATURE [TechDraw::DrawViewDimension] Dimension006
  AngleOverride = false
  Arbitrary = false
  ArbitraryTolerances = false
  EqualTolerance = true
  ExtensionAngle = 0
  FormatSpec = R%.2w
  FormatSpecOverTolerance = %+.2w
  FormatSpecUnderTolerance = %+.2w
  Inverted = false
  LineAngle = 0
  LockPosition = false
  MeasureType = 1
  OverTolerance = 0
  References2D = -> [ProjItem001]
  Rotation = 0
  ScaleType = 0
  TheoreticalExact = false
  Type = 4
  UnderTolerance = 0
  X = -119.885
  Y = -32.2315
FEATURE [TechDraw::DrawViewDimension] Dimension008
  AngleOverride = false
  Arbitrary = false
  ArbitraryTolerances = false
  EqualTolerance = true
  ExtensionAngle = 0
  FormatSpec = %.2w
  FormatSpecOverTolerance = %+.2w
  FormatSpecUnderTolerance = %+.2w
  Inverted = false
  LineAngle = 0
  LockPosition = false
  MeasureType = 1
  OverTolerance = 0
  References2D = -> [ProjItem001]
  Rotation = 0
  ScaleType = 0
  TheoreticalExact = false
  Type = 2
  UnderTolerance = 0
  X = 122.6
  Y = 0.526494
FEATURE [TechDraw::DrawViewDimension] Dimension009
  AngleOverride = false
  Arbitrary = false
  ArbitraryTolerances = false
  EqualTolerance = true
  ExtensionAngle = 0
  FormatSpec = %.2w
  FormatSpecOverTolerance = %+.2w
  FormatSpecUnderTolerance = %+.2w
  Inverted = false
  LineAngle = 0
  LockPosition = false
  MeasureType = 1
  OverTolerance = 0
  References2D = -> [ProjItem001]
  Rotation = 0
  ScaleType = 0
  TheoreticalExact = false
  Type = 2
  UnderTolerance = 0
  X = -116.105
  Y = 2.93058
FEATURE [TechDraw::DrawViewDimension] Dimension010
  AngleOverride = false
  Arbitrary = false
  ArbitraryTolerances = false
  EqualTolerance = true
  ExtensionAngle = 0
  FormatSpec = %.2w
  FormatSpecOverTolerance = %+.2w
  FormatSpecUnderTolerance = %+.2w
  Inverted = false
  LineAngle = 0
  LockPosition = false
  MeasureType = 1
  OverTolerance = 0
  References2D = -> [ProjItem001]
  Rotation = 0
  ScaleType = 0
  TheoreticalExact = false
  Type = 1
  UnderTolerance = 0
  X = -75.283
  Y = -10.4951
FEATURE [TechDraw::DrawViewDimension] Dimension011
  AngleOverride = false
  Arbitrary = false
  ArbitraryTolerances = false
  EqualTolerance = true
  ExtensionAngle = 0
  FormatSpec = %.2w
  FormatSpecOverTolerance = %+.2w
  FormatSpecUnderTolerance = %+.2w
  Inverted = false
  LineAngle = 0
  LockPosition = false
  MeasureType = 1
  OverTolerance = 0
  References2D = -> [ProjItem001]
  Rotation = 0
  ScaleType = 0
  TheoreticalExact = false
  Type = 1
  UnderTolerance = 0
  X = -60
  Y = 21.7689
FEATURE [TechDraw::DrawViewDimension] Dimension012
  AngleOverride = false
  Arbitrary = false
  ArbitraryTolerances = false
  EqualTolerance = true
  ExtensionAngle = 0
  FormatSpec = %.2w
  FormatSpecOverTolerance = %+.2w
  FormatSpecUnderTolerance = %+.2w
  Inverted = false
  LineAngle = 0
  LockPosition = false
  MeasureType = 1
  OverTolerance = 0
  References2D = -> [ProjItem001]
  Rotation = 0
  ScaleType = 0
  TheoreticalExact = false
  Type = 2
  UnderTolerance = 0
  X = -39.4811
  Y = 1.65098
FEATURE [TechDraw::DrawViewDimension] Dimension013
  AngleOverride = false
  Arbitrary = false
  ArbitraryTolerances = false
  EqualTolerance = true
  ExtensionAngle = 0
  FormatSpec = %.2w
  FormatSpecOverTolerance = %+.2w
  FormatSpecUnderTolerance = %+.2w
  Inverted = false
  LineAngle = 0
  LockPosition = false
  MeasureType = 1
  OverTolerance = 0
  References2D = -> [ProjItem001]
  Rotation = 0
  ScaleType = 0
  TheoreticalExact = false
  Type = 1
  UnderTolerance = 0
  X = 101.25
  Y = 1.95724
FEATURE [TechDraw::DrawViewDimension] Dimension014
  AngleOverride = false
  Arbitrary = false
  ArbitraryTolerances = false
  EqualTolerance = true
  ExtensionAngle = 0
  FormatSpec = %.2w
  FormatSpecOverTolerance = %+.2w
  FormatSpecUnderTolerance = %+.2w
  Inverted = false
  LineAngle = 0
  LockPosition = false
  MeasureType = 1
  OverTolerance = 0
  References2D = -> [ProjItem001]
  Rotation = 0
  ScaleType = 0
  TheoreticalExact = false
  Type = 1
  UnderTolerance = 0
  X = -101.816
  Y = 2.47561
FEATURE [TechDraw::DrawViewDimension] Dimension015
  AngleOverride = false
  Arbitrary = false
  ArbitraryTolerances = false
  EqualTolerance = true
  ExtensionAngle = 0
  FormatSpec = %.2w
  FormatSpecOverTolerance = %+.2w
  FormatSpecUnderTolerance = %+.2w
  Inverted = false
  LineAngle = 0
  LockPosition = false
  MeasureType = 1
  OverTolerance = 0
  References2D = -> [ProjItem001]
  Rotation = 0
  ScaleType = 0
  TheoreticalExact = false
  Type = 2
  UnderTolerance = 0
  X = -84.3631
  Y = 40.4283
FEATURE [TechDraw::DrawViewDimension] Dimension016
  AngleOverride = false
  Arbitrary = false
  ArbitraryTolerances = false
  EqualTolerance = true
  ExtensionAngle = 0
  FormatSpec = %.2w
  FormatSpecOverTolerance = %+.2w
  FormatSpecUnderTolerance = %+.2w
  Inverted = false
  LineAngle = 0
  LockPosition = false
  MeasureType = 1
  OverTolerance = 0
  References2D = -> [ProjItem001]
  Rotation = 0
  ScaleType = 0
  TheoreticalExact = false
  Type = 2
  UnderTolerance = 0
  X = -57.1461
  Y = -37.1264
FEATURE [TechDraw::DrawViewDimension] Dimension017
  AngleOverride = false
  Arbitrary = false
  ArbitraryTolerances = false
  EqualTolerance = true
  ExtensionAngle = 0
  FormatSpec = %.2w
  FormatSpecOverTolerance = %+.2w
  FormatSpecUnderTolerance = %+.2w
  Inverted = false
  LineAngle = 0
  LockPosition = false
  MeasureType = 1
  OverTolerance = 0
  References2D = -> [ProjItem001]
  Rotation = 0
  ScaleType = 0
  TheoreticalExact = false
  Type = 1
  UnderTolerance = 0
  X = 0
  Y = 1.53225
FEATURE [TechDraw::DrawViewDimension] Dimension018
  AngleOverride = false
  Arbitrary = false
  ArbitraryTolerances = false
  EqualTolerance = true
  ExtensionAngle = 0
  FormatSpec = %.2w
  FormatSpecOverTolerance = %+.2w
  FormatSpecUnderTolerance = %+.2w
  Inverted = false
  LineAngle = 0
  LockPosition = false
  MeasureType = 1
  OverTolerance = 0
  References2D = -> [ProjItem001]
  Rotation = 0
  ScaleType = 0
  TheoreticalExact = false
  Type = 2
  UnderTolerance = 0
  X = -19.5049
  Y = -13.6792
FEATURE [TechDraw::DrawViewDimension] Dimension019
  AngleOverride = false
  Arbitrary = false
  ArbitraryTolerances = false
  EqualTolerance = true
  ExtensionAngle = 0
  FormatSpec = %.2w
  FormatSpecOverTolerance = %+.2w
  FormatSpecUnderTolerance = %+.2w
  Inverted = false
  LineAngle = 0
  LockPosition = false
  MeasureType = 1
  OverTolerance = 0
  References2D = -> [ProjItem001]
  Rotation = 0
  ScaleType = 0
  TheoreticalExact = false
  Type = 1
  UnderTolerance = 0
  X = 15
  Y = 30.4529
FEATURE [TechDraw::DrawViewDimension] Dimension020
  AngleOverride = false
  Arbitrary = false
  ArbitraryTolerances = false
  EqualTolerance = true
  ExtensionAngle = 0
  FormatSpec = %.2w
  FormatSpecOverTolerance = %+.2w
  FormatSpecUnderTolerance = %+.2w
  Inverted = false
  LineAngle = 0
  LockPosition = false
  MeasureType = 1
  OverTolerance = 0
  References2D = -> [ProjItem001]
  Rotation = 0
  ScaleType = 0
  TheoreticalExact = false
  Type = 2
  UnderTolerance = 0
  X = -1.0969
  Y = 24.1412
FEATURE [TechDraw::DrawViewDimension] Dimension021
  AngleOverride = false
  Arbitrary = false
  ArbitraryTolerances = false
  EqualTolerance = true
  ExtensionAngle = 0
  FormatSpec = ⌀%.2w
  FormatSpecOverTolerance = %+.2w
  FormatSpecUnderTolerance = %+.2w
  Inverted = false
  LineAngle = 0
  LockPosition = false
  MeasureType = 1
  OverTolerance = 0
  References2D = -> [ProjItem001]
  Rotation = 0
  ScaleType = 0
  TheoreticalExact = false
  Type = 5
  UnderTolerance = 0
  X = -119.606
  Y = 26.9114
FEATURE [TechDraw::DrawPage] Page  label="Soporte de botones"
  KeepUpdated = true
  NextBalloonIndex = 1
  ProjectionType = 0
  Template = -> Template
  Views = -> [ProjGroup,Dimension,Dimension001,Dimension002,Dimension003,Dimension004,Dimension005,Dimension006,Dimension008,Dimension009,Dimension010,Dimension011,Dimension012,Dimension013,Dimension014,Dimension015,Dimension016,Dimension017,Dimension018,Dimension019,Dimension020,Dimension021]
